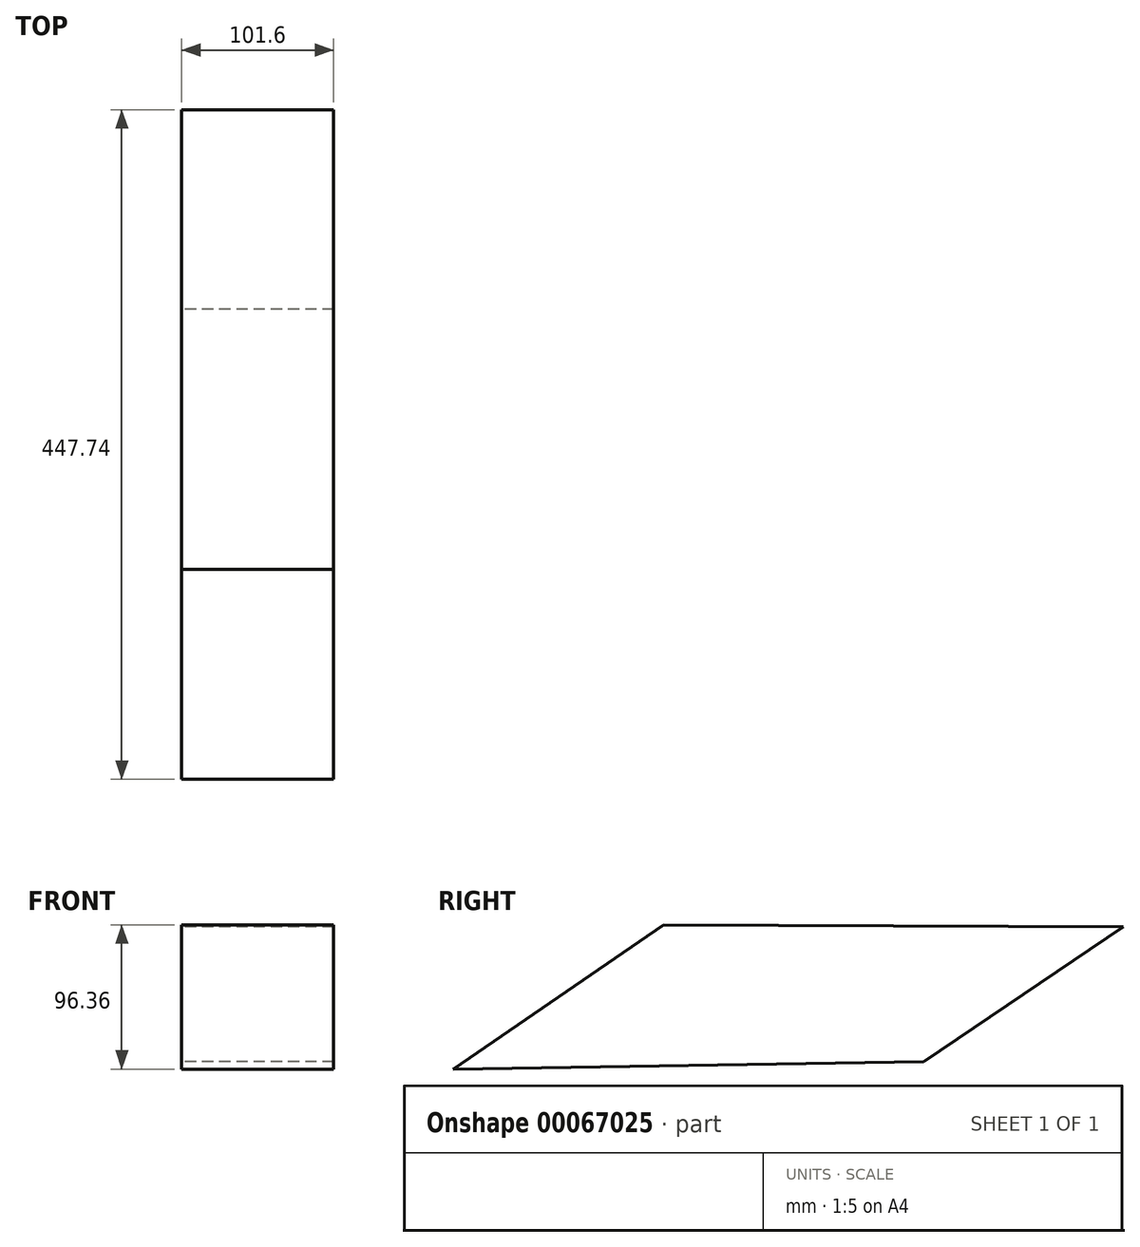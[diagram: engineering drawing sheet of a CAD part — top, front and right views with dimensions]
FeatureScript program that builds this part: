
annotation { "Feature Type Name" : "Feature", "Feature Type Description" : "" }
export const myFeature = defineFeature(function(context is Context, id is Id, definition is map)
    precondition{}
    {
        {
            var Q0;
            Q0=qCreatedBy(makeId("Right.planeOp"),FACE);
            var sketch = newSketch(context, id + "F0", { "sketchPlane" : qUnion([Q0])});
            skLineSegment(sketch, "E0", {"start": v(224.1, 46.85) * mm, "end": v(90.76, -43.29) * mm});
            skLineSegment(sketch, "E1", {"start": v(-83.13, 48.18) * mm, "end": v(-223.63, -48.18) * mm});
            skLineSegment(sketch, "E2", {"start": v(224.1, 46.85) * mm, "end": v(-83.13, 48.18) * mm});
            skLineSegment(sketch, "E3", {"start": v(90.76, -43.29) * mm, "end": v(-223.63, -48.18) * mm});
            skSolve(sketch);
        }
        {
            var Q0;
            Q0=makeQuery(id+"F0.imprint","IMPRINT",FACE,{"disambiguationData":[TD([[makeQuery(id+"F0.imprint","IMPRINT",EDGE,{"derivedFrom":sQuery(id+"F0.wireOp",EDGE,"E0")}),-1.0]])]});
            extrude(context, id + "F1", {"entities" : qUnion([Q0]), "endBound" : BoundingType.SYMMETRIC, "depth" : 101.6 * mm});
        }
    });
